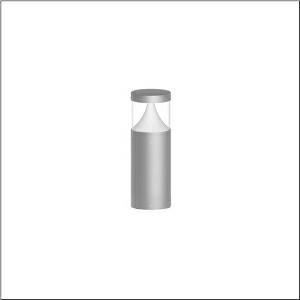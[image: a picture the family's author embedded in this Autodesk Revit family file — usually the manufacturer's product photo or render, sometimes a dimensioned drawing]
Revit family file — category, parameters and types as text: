
# Revit family: cl_31_poller_40_5cl424603
name_source: partatom
category: Lighting Fixtures
units: mm (PartAtom-declared; Revit-internal decimal feet)

## family parameters
Cut with Voids When Loaded = No
Host = Face
Light Source = No
Part Type = Normal
Room Calculation Point = No
Round Connector Dimension = Use Diameter
Shared = No

## types (1)
- --- (1 x LED, 800 lm, 7.2 W, 3000K)
    Apparent Load = 7 VA
    CIE Flux Codes = 19 66 88 92 100
    Color Rendering = 80
    Color Temperature = 3000K
    Default Elevation = 1800 mm
    Description = CL 31 Bollard 40, bollard luminaire, primary light control with lens, of PC, primary optical cover: cover panel, of PC, transparent, secondary light control with reflector, of PC, primary light characteristic: asymmetric, LED, rated luminous flux: 800lm, luminous efficacy: 110lm/W, light colour: 830, colour temperature: 3000K, control gear: DALI, with terminal, 5-pole, max. 2.5mm², mains connection: 220..240V, AC, 50/60Hz, rated input power: 7.2W, luminaire housing, of aluminium, powder-coated, SITECO metallic grey, diameter: 170mm, height: 400mm, protection rating (complete): IP65, insulation class (complete): insulation class I (protective earthing), certification: CE, ENEC, impact resistance: IK10, permissible operating ambient temperature for outdoor applications: -20..+50°C, packaging unit: 1 piece
    Height = 200 mm  [stored 0.656168 ft]
    Lamp = 1 x LED
    Lamp Light Flux = 800 lm
    Lamp Power = 7.2 W
    Lamp count = 1
    Length = 170 mm  [stored 0.557743 ft]
    Luminous efficacy = 111 lm/W
    Manufacturer = Siteco
    ModVariant = No
    Model = 5CL424603
    Mounting Place = Floor
    Mounting Type = Freestanding
    Number of Poles = 1
    OnlyDefault = Yes
    Power Factor = 1
    Product Name = CL 31 Poller 40
    Product group = bollard luminaire
    ProductGroupID = 1304
    Protection Class = Protection class I
    Protection Degree = IP 65
    RLX_Detail_Level = 1
    RLX_Emergency_Light_Flux = 0 lm
    RLX_Emergency_Type = 0
    RLX_Emergency_Type_DB = No
    RlxData = <blob elided: 61649 chars, md5=7c790a27>
    Socket = socket
    Standby Power = 0 W
    System Light Flux = 800 lm
    System Power = 7 W
    Type Comments = factory setting: luminous flux: 100 % | dim-lin: 254 | 182 mA
    Type Image = l_1006907.jpg
    URL = http://relux.com
    VarID = @adj_192777
    Voltage = 0 V
    Weight = 0.00 kg
    Width = 0 mm  [stored 0 ft]

note: [stored X ft] marks values corroborated as IEEE doubles in the binary element streams (Revit-internal decimal feet)

## geometry (parser evidence)
native form markers: Blend x4, Sweep x15
no freeform markers — native parametric forms only
